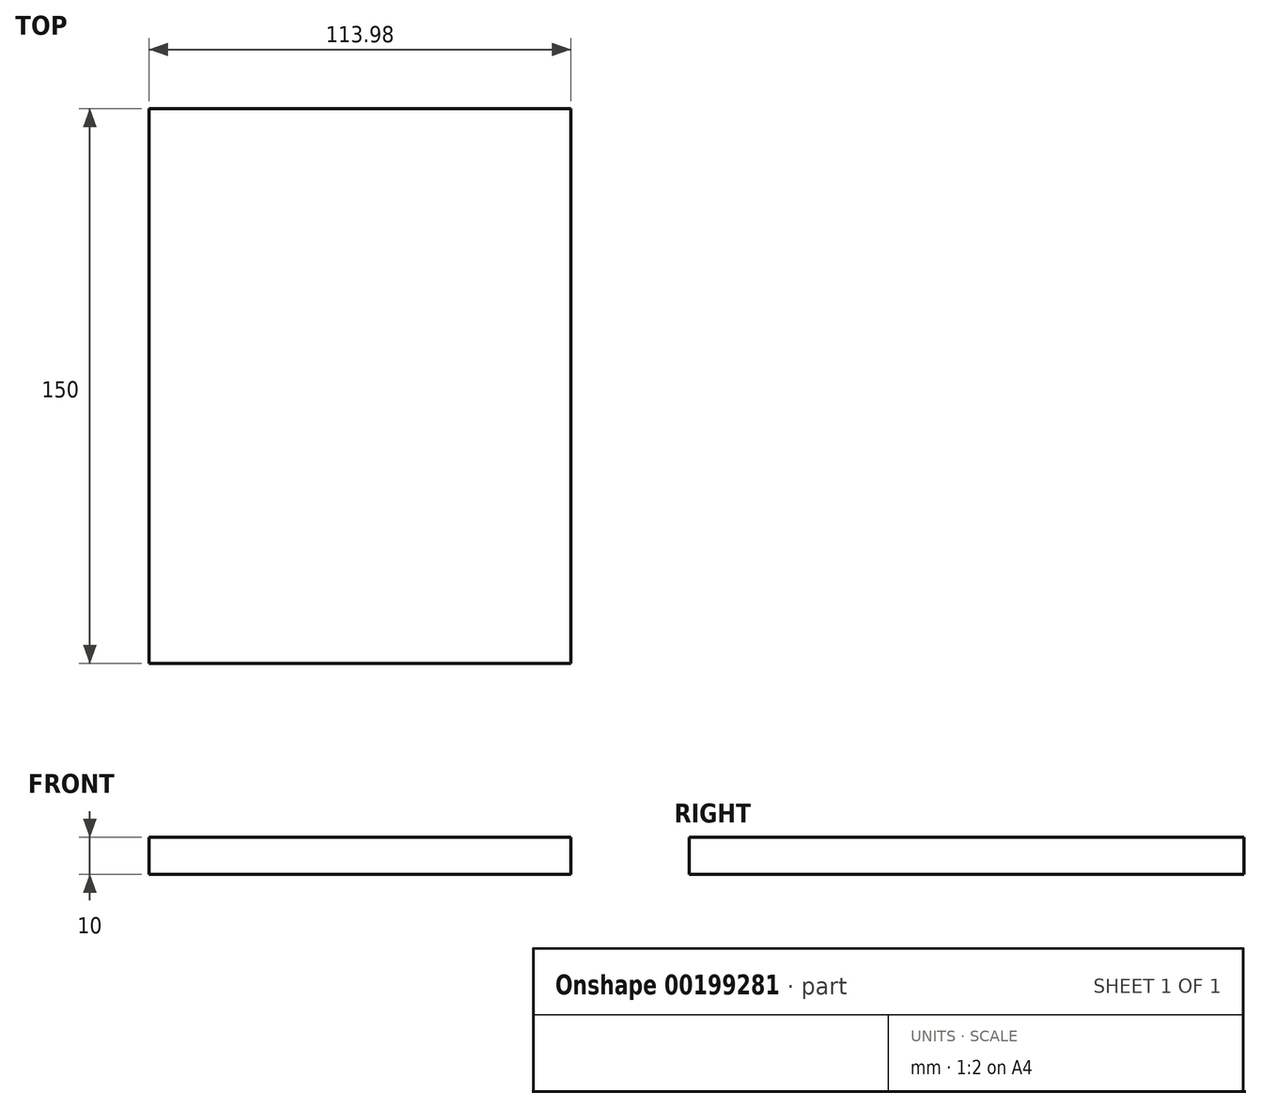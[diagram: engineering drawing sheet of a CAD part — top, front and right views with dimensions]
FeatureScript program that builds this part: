
annotation { "Feature Type Name" : "Feature", "Feature Type Description" : "" }
export const myFeature = defineFeature(function(context is Context, id is Id, definition is map)
    precondition{}
    {
        {
            var Q0;
            Q0=qCreatedBy(makeId("Top.planeOp"),FACE);
            var sketch = newSketch(context, id + "F0", { "sketchPlane" : qUnion([Q0])});
            skLineSegment(sketch, "E0.bottom", {"start": v(-57, 75) * mm, "end": v(57, 75) * mm});
            skLineSegment(sketch, "E0.top", {"start": v(-57, -75) * mm, "end": v(57, -75) * mm});
            skLineSegment(sketch, "E0.left", {"start": v(-57, 75) * mm, "end": v(-57, -75) * mm});
            skLineSegment(sketch, "E0.right", {"start": v(57, 75) * mm, "end": v(57, -75) * mm});
            skPoint(sketch, "E0.middle", {"position": v(0, 0) * mm});
            skSolve(sketch);
        }
        {
            var Q0;
            Q0=makeQuery(id+"F0.imprint","IMPRINT",FACE,{"disambiguationData":[TD([[makeQuery(id+"F0.imprint","IMPRINT",EDGE,{"derivedFrom":sQuery(id+"F0.wireOp",EDGE,"E0.bottom")}),-1.0]])]});
            extrude(context, id + "F1", {"entities" : qUnion([Q0]), "depth" : 10 * mm});
        }
    });
